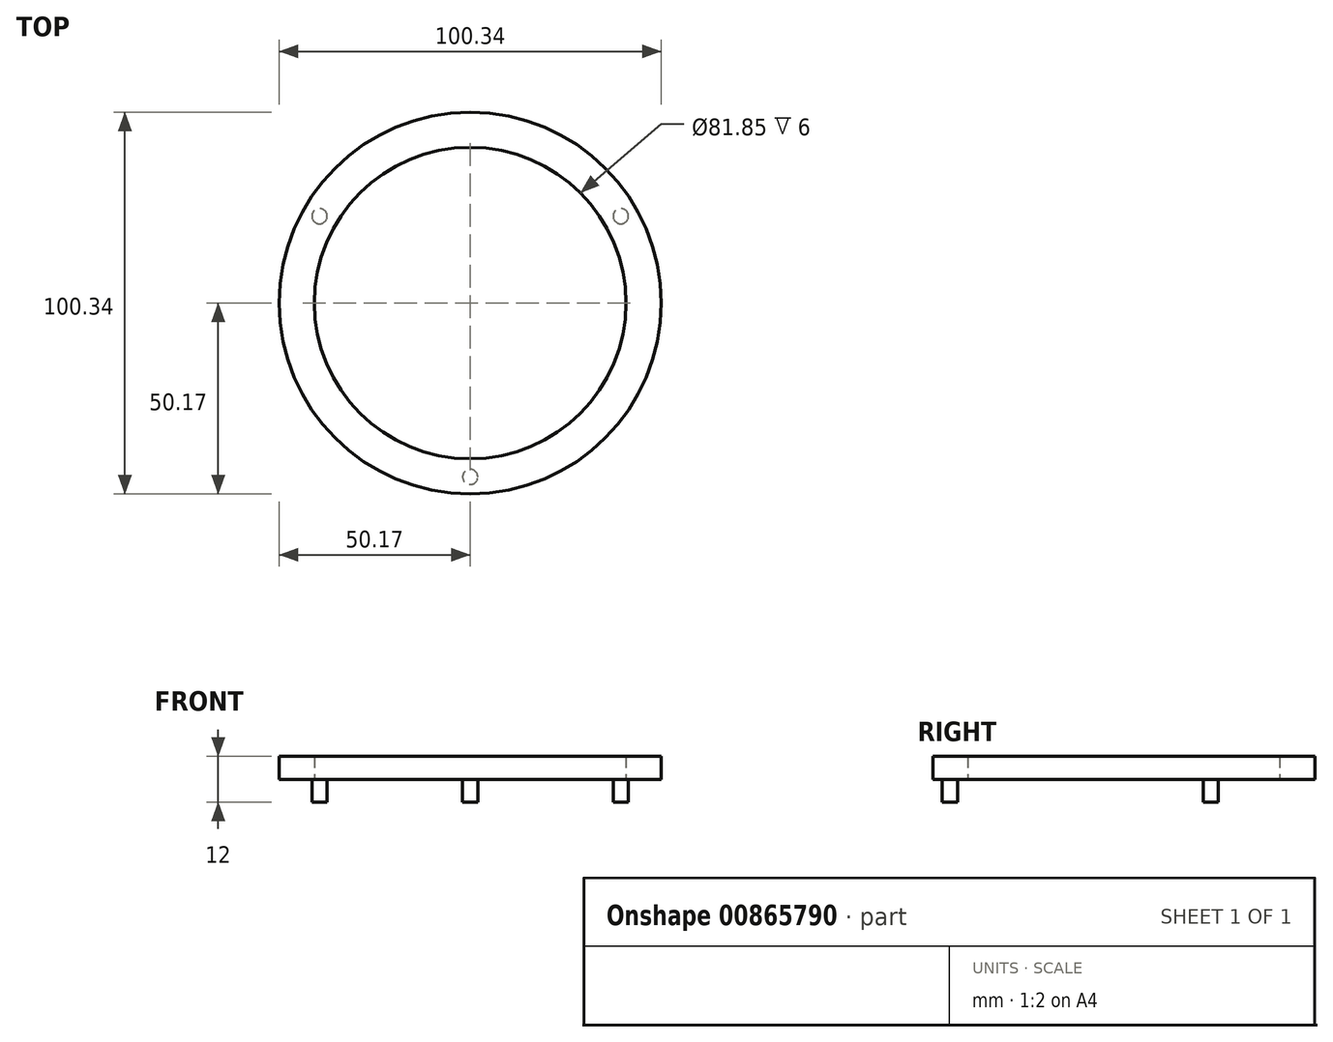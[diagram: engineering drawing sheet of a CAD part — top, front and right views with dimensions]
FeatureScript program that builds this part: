
annotation { "Feature Type Name" : "Feature", "Feature Type Description" : "" }
export const myFeature = defineFeature(function(context is Context, id is Id, definition is map)
    precondition{}
    {
        {
            var Q0;
            Q0=qCreatedBy(makeId("Top.planeOp"),FACE);
            var sketch = newSketch(context, id + "F0", { "sketchPlane" : qUnion([Q0])});
            skCircle(sketch, "E0", {"center": v(0, 0) * mm, "radius": 50.17 * mm});
            skCircle(sketch, "E1", {"center": v(0, 0) * mm, "radius": 40.93 * mm});
            skSolve(sketch);
        }
        {
            var Q0;
            Q0=makeQuery(id+"F0.imprint","IMPRINT",FACE,{"disambiguationData":[TD([[makeQuery(id+"F0.imprint","IMPRINT",EDGE,{"derivedFrom":sQuery(id+"F0.wireOp",EDGE,"E0")}),1.0]])]});
            extrude(context, id + "F1", {"entities" : qUnion([Q0]), "depth" : 6 * mm, "offsetDistance" : 25 * mm});
        }
        {
            var Q0;
            Q0=makeQuery(id+"F1.opExtrude","CAP_FACE",FACE,{"disambiguationData":[OSD([sQuery(id+"F0.wireOp",EDGE,"E0"),sQuery(id+"F0.wireOp",EDGE,"E1")])],"isStart":true});
            var sketch = newSketch(context, id + "F2", { "sketchPlane" : qUnion([Q0])});
            skCircle(sketch, "E2", {"center": v(0, 45.68) * mm, "radius": 2 * mm});
            skCircle(sketch, "E3.1.0", {"center": v(39.56, -22.84) * mm, "radius": 2 * mm});
            skCircle(sketch, "E3.2.0", {"center": v(-39.56, -22.84) * mm, "radius": 2 * mm});
            skPoint(sketch, "E3.center", {"position": v(0, 0) * mm});
            skLineSegment(sketch, "E3.anchor1", {"start": v(0, 0) * mm, "end": v(0, 45.68) * mm, "construction": true});
            skLineSegment(sketch, "E3.anchor2", {"start": v(0, 0) * mm, "end": v(-39.56, -22.84) * mm, "construction": true});
            skSolve(sketch);
        }
        {
            var Q0;
            Q0=makeQuery(id+"F2.imprint","IMPRINT",FACE,{"disambiguationData":[TD([[makeQuery(id+"F2.imprint","IMPRINT",EDGE,{"derivedFrom":sQuery(id+"F2.wireOp",EDGE,"E2")}),1.0]])]});
            var Q1;
            Q1=makeQuery(id+"F2.imprint","IMPRINT",FACE,{"disambiguationData":[TD([[makeQuery(id+"F2.imprint","IMPRINT",EDGE,{"derivedFrom":sQuery(id+"F2.wireOp",EDGE,"E3.2.0")}),1.0]])]});
            var Q2;
            Q2=makeQuery(id+"F2.imprint","IMPRINT",FACE,{"disambiguationData":[TD([[makeQuery(id+"F2.imprint","IMPRINT",EDGE,{"derivedFrom":sQuery(id+"F2.wireOp",EDGE,"E3.1.0")}),1.0]])]});
            extrude(context, id + "F3", {"entities" : qUnion([Q0, Q1, Q2]), "operationType" : NewBodyOperationType.ADD, "depth" : 6 * mm, "offsetDistance" : 25 * mm});
        }
    });
